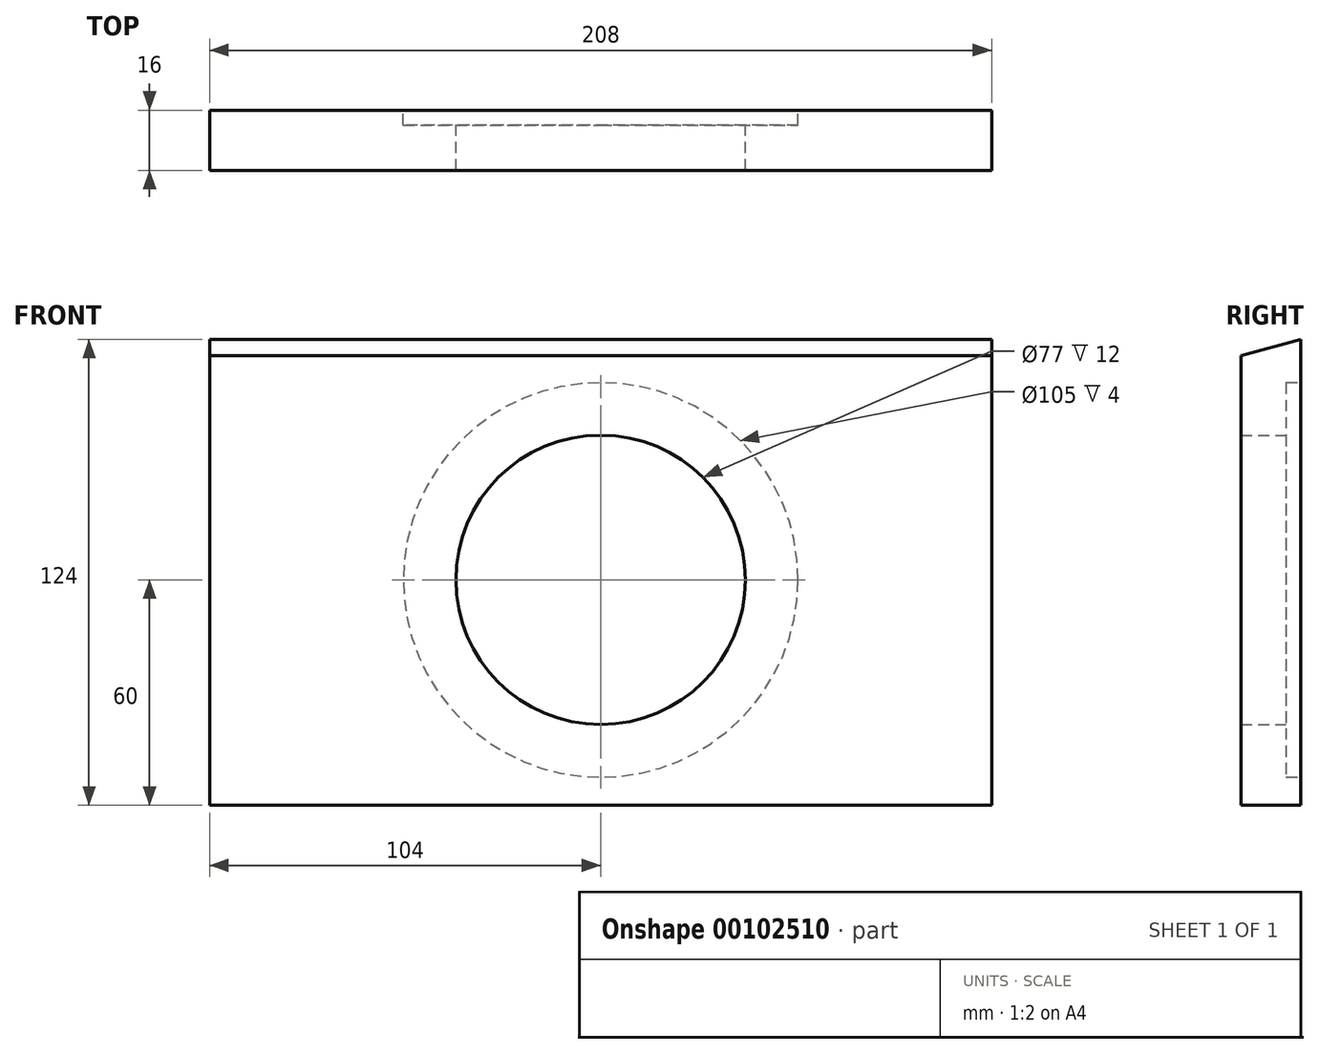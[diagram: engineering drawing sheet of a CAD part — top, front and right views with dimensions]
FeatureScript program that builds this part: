
annotation { "Feature Type Name" : "Feature", "Feature Type Description" : "" }
export const myFeature = defineFeature(function(context is Context, id is Id, definition is map)
    precondition{}
    {
        {
            var Q0;
            Q0=qCreatedBy(makeId("Front.planeOp"),FACE);
            var sketch = newSketch(context, id + "F0", { "sketchPlane" : qUnion([Q0])});
            skLineSegment(sketch, "E0.bottom", {"start": v(0, 0) * mm, "end": v(208, 0) * mm});
            skLineSegment(sketch, "E0.top", {"start": v(0, 124) * mm, "end": v(208, 124) * mm});
            skLineSegment(sketch, "E0.left", {"start": v(0, 0) * mm, "end": v(0, 124) * mm});
            skLineSegment(sketch, "E0.right", {"start": v(208, 0) * mm, "end": v(208, 124) * mm});
            skSolve(sketch);
        }
        {
            var Q0;
            Q0=qSketchRegion(id+"F0",true);
            extrude(context, id + "F1", {"entities" : qUnion([Q0]), "depth" : 16 * mm});
        }
        {
            var Q0;
            Q0=qCreatedBy(makeId("Right.planeOp"),FACE);
            var sketch = newSketch(context, id + "F2", { "sketchPlane" : qUnion([Q0])});
            skLineSegment(sketch, "E1", {"start": v(0, 124) * mm, "end": v(-16, 124) * mm});
            skLineSegment(sketch, "E2", {"start": v(-16, 124) * mm, "end": v(-16, 119.71) * mm});
            skLineSegment(sketch, "E3", {"start": v(-16, 119.71) * mm, "end": v(0, 124) * mm});
            skSolve(sketch);
        }
        {
            var Q0;
            Q0=qSketchRegion(id+"F2",true);
            var Q1;
            Q1=makeQuery(id+"F1.opExtrude","SWEPT_FACE",FACE,{"disambiguationData":[OSD([sQuery(id+"F0.wireOp",EDGE,"E0.right")])]});
            extrude(context, id + "F3", {"entities" : qUnion([Q0]), "operationType" : NewBodyOperationType.REMOVE, "endBoundEntityFace" : qUnion([Q1]), "depth" : 240 * mm});
        }
        {
            var Q0;
            Q0=makeQuery(id+"F1.opExtrude","CAP_FACE",FACE,{"disambiguationData":[OSD([sQuery(id+"F0.wireOp",EDGE,"E0.bottom"),sQuery(id+"F0.wireOp",EDGE,"E0.top"),sQuery(id+"F0.wireOp",EDGE,"E0.left"),sQuery(id+"F0.wireOp",EDGE,"E0.right")])],"isStart":true});
            var sketch = newSketch(context, id + "F4", { "sketchPlane" : qUnion([Q0])});
            skPoint(sketch, "E4", {"position": v(-104, 60) * mm});
            skLineSegment(sketch, "E5", {"start": v(-104, 0) * mm, "end": v(-104, 120) * mm, "construction": true});
            skPoint(sketch, "E6", {"position": v(-104, 124) * mm});
            skSolve(sketch);
        }
        {
            var Q0;
            Q0=sQuery(id+"F4.wireOp",VERTEX,"E4");
            var Q1;
            Q1=makeQuery(id+"F1.opExtrude","SWEPT_BODY",BODY,{"disambiguationData":[OSD([sQuery(id+"F0.wireOp",EDGE,"E0.bottom"),sQuery(id+"F0.wireOp",EDGE,"E0.top"),sQuery(id+"F0.wireOp",EDGE,"E0.left"),sQuery(id+"F0.wireOp",EDGE,"E0.right")])]});
            hole(context, id + "F5", {"style" : HoleStyle.SIMPLE, "endStyle" : HoleEndStyle.THROUGH, "holeDiameter" : 77 * mm, "locations" : qUnion([Q0]), "scope" : qUnion([Q1]), "isTappedThrough" : true});
        }
        {
            var Q0;
            Q0=makeQuery(id+"F1.opExtrude","CAP_FACE",FACE,{"disambiguationData":[OSD([sQuery(id+"F0.wireOp",EDGE,"E0.bottom"),sQuery(id+"F0.wireOp",EDGE,"E0.top"),sQuery(id+"F0.wireOp",EDGE,"E0.left"),sQuery(id+"F0.wireOp",EDGE,"E0.right")])],"isStart":true});
            var sketch = newSketch(context, id + "F6", { "sketchPlane" : qUnion([Q0])});
            skCircle(sketch, "E7", {"center": v(-104, 60) * mm, "radius": 52.5 * mm});
            skSolve(sketch);
        }
        {
            var Q0;
            Q0 = qSketchRegion(id + "F6", true);
            extrude(context, id + "F7", {"entities" : qUnion([Q0]), "operationType" : NewBodyOperationType.REMOVE, "oppositeDirection" : true, "depth" : 4 * mm});
        }
    });
